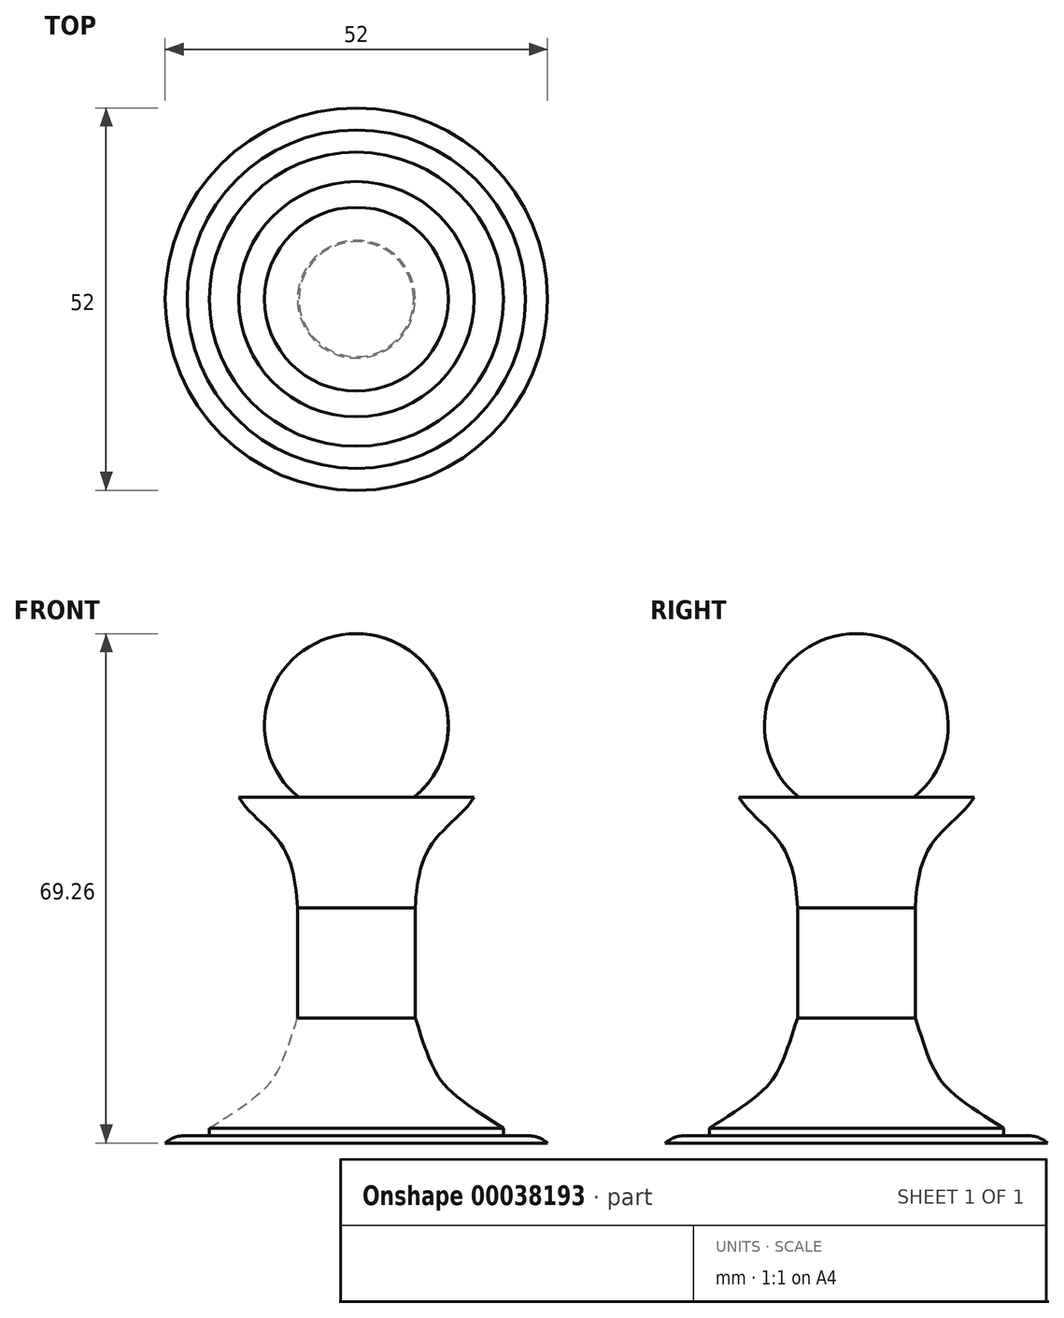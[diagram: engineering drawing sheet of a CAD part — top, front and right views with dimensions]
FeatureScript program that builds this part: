
annotation { "Feature Type Name" : "Feature", "Feature Type Description" : "" }
export const myFeature = defineFeature(function(context is Context, id is Id, definition is map)
    precondition{}
    {
        {
            var Q0;
            Q0=qCreatedBy(makeId("Front.planeOp"),FACE);
            var sketch = newSketch(context, id + "F0", { "sketchPlane" : qUnion([Q0])});
            skArc(sketch, "E0", {"start": v(5.55, 20.5) * mm, "mid": v(9.54, 34.4) * mm, "end": v(-2.26, 42.76) * mm});
            skLineSegment(sketch, "E1", {"start": v(-2.26, 30.5) * mm, "end": v(-2.26, 20.5) * mm});
            skLineSegment(sketch, "E2", {"start": v(5.55, 20.5) * mm, "end": v(13.74, 20.5) * mm});
            skLineSegment(sketch, "E3", {"start": v(-2.26, 20.5) * mm, "end": v(-2.26, 5.5) * mm});
            skLineSegment(sketch, "E4", {"start": v(5.74, 5.5) * mm, "end": v(5.74, -9.5) * mm});
            skLineSegment(sketch, "E5", {"start": v(-2.26, -9.5) * mm, "end": v(-2.26, -24.5) * mm});
            skLineSegment(sketch, "E6", {"start": v(-2.26, -24.5) * mm, "end": v(-2.26, -26.5) * mm});
            skLineSegment(sketch, "E7", {"start": v(17.74, -25.5) * mm, "end": v(20.74, -25.5) * mm});
            skLineSegment(sketch, "E8", {"start": v(-2.26, -26.5) * mm, "end": v(23.74, -26.5) * mm});
            skFitSpline(sketch, "E9", {"points": [v(13.74, 20.5) * mm, v(7.79, 13.85) * mm, v(5.74, 5.5) * mm], "startDerivative": vector(-9.28, -14.75) * mm, "endDerivative": vector(-0.9, -16.13) * mm});
            skFitSpline(sketch, "E10", {"points": [v(5.74, -9.5) * mm, v(8.14, -16.14) * mm, v(17.74, -24.5) * mm], "startDerivative": vector(3.83, -10.8) * mm, "endDerivative": vector(34.1, -21.69) * mm});
            skLineSegment(sketch, "E11", {"start": v(17.74, -24.5) * mm, "end": v(17.74, -25.5) * mm});
            skFitSpline(sketch, "E12", {"points": [v(20.74, -25.5) * mm, v(22.41, -25.72) * mm, v(23.74, -26.5) * mm], "startDerivative": vector(3.4, -0.14) * mm, "endDerivative": vector(2.59, -1.87) * mm});
            skLineSegment(sketch, "E13", {"start": v(-2.26, 30.26) * mm, "end": v(-2.26, 42.76) * mm});
            skPoint(sketch, "E14.orphan", {"position": v(-2.26, -25.5) * mm});
            skLineSegment(sketch, "E15", {"start": v(-2.26, 5.5) * mm, "end": v(-2.26, -9.5) * mm});
            skSolve(sketch);
        }
        {
            var Q0;
            {var subQ2=sQuery(id+"F0.wireOp",EDGE,"E0");Q0=makeQuery(id+"F0.imprint","IMPRINT",FACE,{"disambiguationData":[TD([[makeQuery(id+"F0.imprint","IMPRINT",EDGE,{"derivedFrom":subQ2}),1.0]])]});}
            var Q1;
            Q1=sQuery(id+"F0.wireOp",EDGE,"E3");
            revolve(context, id + "F1", {"entities" : qUnion([Q0]), "axis" : qUnion([Q1]), "revolveType" : RevolveType.FULL});
        }
    });
